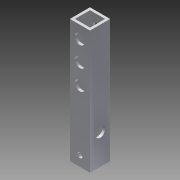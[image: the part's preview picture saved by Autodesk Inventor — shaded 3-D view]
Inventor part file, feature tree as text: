
AUTODESK INVENTOR PART (.ipt)
format: ipt  version: 2015 (Build 190159000, 159)  size: 122,880 bytes
history: native  units: in
note: dims shown in document units (in); Inventor stores cm internally (conversion verified against a paired STEP export)
features: sketch x4, extrude x2, hole x2
ambient origin geometry x8: Origin, YZ Plane, XZ Plane, XY Plane, X Axis, Y Axis, Z Axis, Center Point
bodies: Solid1 (feature_tree)
feature tree (8):
  extrude  "Extrusion1"  Depth=1.0in
  hole  "Hole1"  [1 undecoded]
  hole  "Hole2"  [1 undecoded]
  extrude  "Extrusion2"  Depth=1.0in
  sketch  "Sketch1"  dims[d0=1.0in d1=1.0in]
  sketch  "Sketch2"  dims[d2=0.75in d3=0.75in]
  sketch  "Sketch3"  dims[d4=0.125in d5=0.125in]
  sketch  "Sketch6"  dims[d6=6.125in d7=0.0in d8=0.5in d9=0.5in d10=0.5in d11=0.5in d14=0.25in d15=0.75in d16=0.375in d17=0.25in d18=0.5635in d19=1.0in d20=0.8108in d21=0.5in d22=1.5in d23=0.375in d24=0.75in d25=0.375in d26=0.25in d27=0.5635in d28=1.0in d29=0.8108in d54=0.5in d55=0.5in d56=0.0in]
note: 2 required parameter values undecoded (feature->parameter linkage not recoverable at this tier; creation-order binding heuristic only, values carry confidence <= 0.55)
